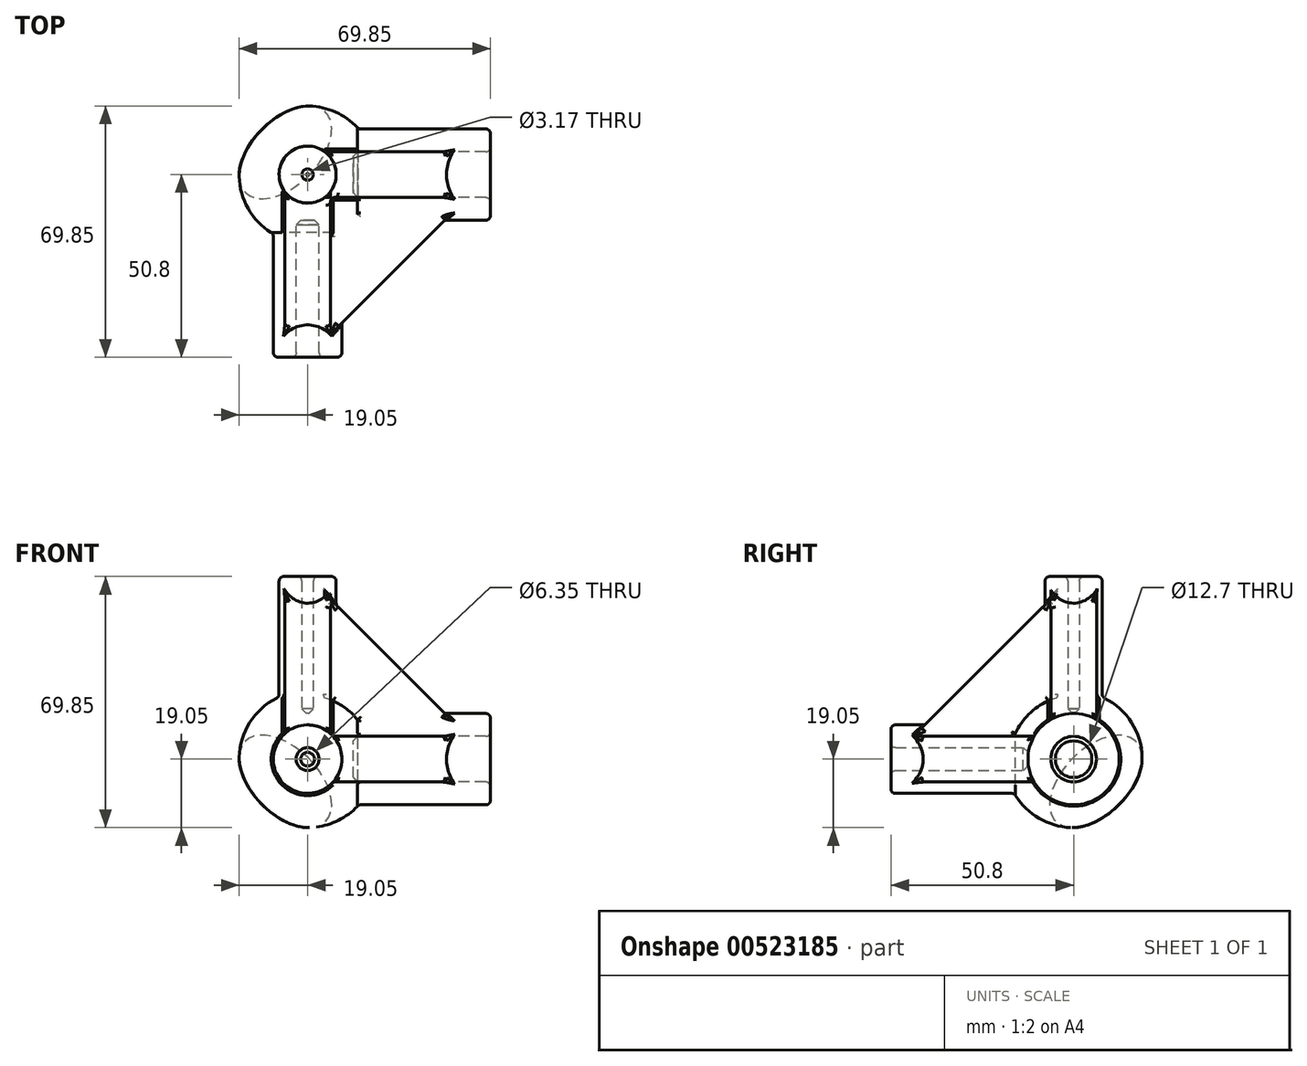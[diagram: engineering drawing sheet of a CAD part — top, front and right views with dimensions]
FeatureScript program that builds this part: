
annotation { "Feature Type Name" : "Feature", "Feature Type Description" : "" }
export const myFeature = defineFeature(function(context is Context, id is Id, definition is map)
    precondition{}
    {
        {
            var Q0;
            Q0=qCreatedBy(makeId("Right.planeOp"),FACE);
            var sketch = newSketch(context, id + "F0", { "sketchPlane" : qUnion([Q0])});
            skLineSegment(sketch, "E0", {"start": v(0, 0) * mm, "end": v(0, 19.05) * mm});
            skLineSegment(sketch, "E1", {"start": v(0, 0) * mm, "end": v(0, -19.05) * mm});
            skLineSegment(sketch, "E2", {"start": v(0, 0) * mm, "end": v(-19.05, 0) * mm});
            skArc(sketch, "E3", {"start": v(0, 19.05) * mm, "mid": v(-19.05, 0) * mm, "end": v(0, -19.05) * mm});
            skSolve(sketch);
        }
        {
            var Q0;
            Q0 = qSketchRegion(id + "F0", true);
            var Q1;
            Q1=sQuery(id+"F0.wireOp",EDGE,"E0");
            revolve(context, id + "F1", {"entities" : qUnion([Q0]), "axis" : qUnion([Q1]), "revolveType" : RevolveType.FULL});
        }
        {
            var Q0;
            Q0=qCreatedBy(makeId("Front.planeOp"),FACE);
            var sketch = newSketch(context, id + "F2", { "sketchPlane" : qUnion([Q0])});
            skCircle(sketch, "E4", {"center": v(0, 0) * mm, "radius": 3.18 * mm});
            skCircle(sketch, "E5.0", {"center": v(0, 0) * mm, "radius": 9.52 * mm});
            skSolve(sketch);
        }
        {
            var Q0;
            Q0 = qSketchRegion(id + "F2", true);
            extrude(context, id + "F3", {"entities" : qUnion([Q0]), "operationType" : NewBodyOperationType.ADD, "depth" : 50.8 * mm, "offsetDistance" : 25.4 * mm});
        }
        {
            var Q0;
            Q0=qCreatedBy(makeId("Right.planeOp"),FACE);
            var sketch = newSketch(context, id + "F4", { "sketchPlane" : qUnion([Q0])});
            skCircle(sketch, "E6", {"center": v(0, 0) * mm, "radius": 6.35 * mm});
            skCircle(sketch, "E7.0", {"center": v(0, 0) * mm, "radius": 12.7 * mm});
            skSolve(sketch);
        }
        {
            var Q0;
            Q0 = qSketchRegion(id + "F4", true);
            extrude(context, id + "F5", {"entities" : qUnion([Q0]), "operationType" : NewBodyOperationType.ADD, "depth" : 50.8 * mm, "offsetDistance" : 25.4 * mm});
        }
        {
            var Q0;
            Q0=qCreatedBy(makeId("Top.planeOp"),FACE);
            var sketch = newSketch(context, id + "F6", { "sketchPlane" : qUnion([Q0])});
            skCircle(sketch, "E8", {"center": v(0, 0) * mm, "radius": 1.59 * mm});
            skCircle(sketch, "E9.0", {"center": v(0, 0) * mm, "radius": 7.94 * mm});
            skSolve(sketch);
        }
        {
            var Q0;
            Q0 = qSketchRegion(id + "F6", true);
            extrude(context, id + "F7", {"entities" : qUnion([Q0]), "operationType" : NewBodyOperationType.ADD, "depth" : 50.8 * mm, "offsetDistance" : 25.4 * mm});
        }
        {
            var Q0;
            Q0=makeQuery(id+"F7.opExtrude","CAP_FACE",FACE,{"disambiguationData":[OSD([sQuery(id+"F6.wireOp",EDGE,"E8"),sQuery(id+"F6.wireOp",EDGE,"E9.0")])],"isStart":false});
            cPlane(context, id + "F8", {"entities" : qUnion([Q0]), "cplaneType" : CPlaneType.OFFSET, "offset" : 0 * mm, "width" : 152.4 * mm, "height" : 152.4 * mm});
        }
        {
            var Q0;
            Q0=qCreatedBy(id+"F8.planeOp",FACE);
            var sketch = newSketch(context, id + "F9", { "sketchPlane" : qUnion([Q0])});
            skCircle(sketch, "E10", {"center": v(0, 0) * mm, "radius": 1.59 * mm});
            skSolve(sketch);
        }
        {
            var Q0;
            Q0=makeQuery(id+"F5.opExtrude","CAP_FACE",FACE,{"disambiguationData":[OSD([sQuery(id+"F4.wireOp",EDGE,"E6"),sQuery(id+"F4.wireOp",EDGE,"E7.0")])],"isStart":false});
            cPlane(context, id + "F10", {"entities" : qUnion([Q0]), "cplaneType" : CPlaneType.OFFSET, "offset" : 0 * mm, "width" : 152.4 * mm, "height" : 152.4 * mm});
        }
        {
            var Q0;
            Q0=qCreatedBy(id+"F10.planeOp",FACE);
            var sketch = newSketch(context, id + "F11", { "sketchPlane" : qUnion([Q0])});
            skCircle(sketch, "E11", {"center": v(0, 0) * mm, "radius": 6.35 * mm});
            skSolve(sketch);
        }
        {
            var Q0;
            Q0=makeQuery(id+"F3.opExtrude","CAP_FACE",FACE,{"disambiguationData":[OSD([sQuery(id+"F2.wireOp",EDGE,"E4"),sQuery(id+"F2.wireOp",EDGE,"E5.0")])],"isStart":false});
            cPlane(context, id + "F12", {"entities" : qUnion([Q0]), "cplaneType" : CPlaneType.OFFSET, "offset" : 0 * mm, "width" : 152.4 * mm, "height" : 152.4 * mm});
        }
        {
            var Q0;
            Q0=qCreatedBy(id+"F12.planeOp",FACE);
            var sketch = newSketch(context, id + "F13", { "sketchPlane" : qUnion([Q0])});
            skCircle(sketch, "E12", {"center": v(0, 0) * mm, "radius": 3.18 * mm});
            skSolve(sketch);
        }
        {
            var Q0;
            Q0=qCreatedBy(makeId("Top.planeOp"),FACE);
            var sketch = newSketch(context, id + "F14", { "sketchPlane" : qUnion([Q0])});
            skLineSegment(sketch, "E13", {"start": v(0, 0) * mm, "end": v(0, 63.5) * mm});
            skLineSegment(sketch, "E14", {"start": v(0, 0) * mm, "end": v(-63.5, 0) * mm});
            skSolve(sketch);
        }
        {
            var Q0;
            Q0=qCreatedBy(makeId("Right.planeOp"),FACE);
            var sketch = newSketch(context, id + "F15", { "sketchPlane" : qUnion([Q0])});
            skPoint(sketch, "E15.0", {"position": v(63.5, 0) * mm});
            skLineSegment(sketch, "E16", {"start": v(0, 0) * mm, "end": v(63.5, 0) * mm});
            skLineSegment(sketch, "E17", {"start": v(0, 0) * mm, "end": v(0, -63.5) * mm});
            skSolve(sketch);
        }
        {
            var Q0;
            Q0=sQuery(id+"F14.wireOp",VERTEX,"E14.end");
            var Q1;
            Q1=sQuery(id+"F15.wireOp",VERTEX,"E15.0");
            var Q2;
            Q2=sQuery(id+"F15.wireOp",VERTEX,"E17.end");
            cPlane(context, id + "F16", {"entities" : qUnion([Q0, Q1, Q2]), "cplaneType" : CPlaneType.THREE_POINT, "offset" : 25.4 * mm, "width" : 152.4 * mm, "height" : 152.4 * mm});
        }
        {
            var Q0;
            Q0=qCreatedBy(id+"F16.planeOp",FACE);
            var sketch = newSketch(context, id + "F17", { "sketchPlane" : qUnion([Q0])});
            skCircle(sketch, "E18", {"center": v(0, 0) * mm, "radius": 25.4 * mm});
            skSolve(sketch);
        }
        {
            var Q0;
            Q0=qCreatedBy(makeId("Top.planeOp"),FACE);
            var sketch = newSketch(context, id + "F18", { "sketchPlane" : qUnion([Q0])});
            skLineSegment(sketch, "E19", {"start": v(0, 0) * mm, "end": v(50.8, 0) * mm});
            skLineSegment(sketch, "E20", {"start": v(0, 0) * mm, "end": v(0, -50.8) * mm});
            skLineSegment(sketch, "E21", {"start": v(50.8, 0) * mm, "end": v(0, -50.8) * mm});
            skSolve(sketch);
        }
        {
            var Q0;
            Q0=makeQuery(id+"F18.imprint","IMPRINT",FACE,{"disambiguationData":[TD([[makeQuery(id+"F18.imprint","IMPRINT",EDGE,{"derivedFrom":sQuery(id+"F18.wireOp",EDGE,"E19")}),-1.0]])]});
            extrude(context, id + "F19", {"entities" : qUnion([Q0]), "operationType" : NewBodyOperationType.ADD, "depth" : 6.35 * mm, "offsetDistance" : 25.4 * mm, "hasDraft" : true, "draftAngle" : 0 * degree, "hasSecondDirection" : true, "secondDirectionOppositeDirection" : true, "secondDirectionDepth" : 6.35 * mm});
        }
        {
            var Q0;
            Q0=makeQuery(id+"F17.imprint","IMPRINT",FACE,{"disambiguationData":[TD([[makeQuery(id+"F17.imprint","IMPRINT",EDGE,{"derivedFrom":sQuery(id+"F17.wireOp",EDGE,"E18")}),1.0]])]});
            extrude(context, id + "F20", {"entities" : qUnion([Q0]), "operationType" : NewBodyOperationType.REMOVE, "depth" : 25.4 * mm, "offsetDistance" : 25.4 * mm});
        }
        {
            var Q0;
            Q0=qCreatedBy(makeId("Right.planeOp"),FACE);
            var sketch = newSketch(context, id + "F21", { "sketchPlane" : qUnion([Q0])});
            skLineSegment(sketch, "E22", {"start": v(0, 0) * mm, "end": v(0, 50.8) * mm});
            skLineSegment(sketch, "E23.0", {"start": v(0, 0) * mm, "end": v(-50.8, 0) * mm});
            skLineSegment(sketch, "E24", {"start": v(0, 50.8) * mm, "end": v(-50.8, 0) * mm});
            skPoint(sketch, "E25.0", {"position": v(0, 0) * mm});
            skLineSegment(sketch, "E26.0", {"start": v(-7.94, 50.8) * mm, "end": v(7.94, 50.8) * mm});
            skLineSegment(sketch, "E26.1", {"start": v(-7.94, 17.32) * mm, "end": v(7.94, 17.32) * mm});
            skSolve(sketch);
        }
        {
            var Q0;
            Q0 = qSketchRegion(id + "F21", true);
            extrude(context, id + "F22", {"entities" : qUnion([Q0]), "operationType" : NewBodyOperationType.ADD, "depth" : 6.35 * mm, "offsetDistance" : 25.4 * mm, "hasSecondDirection" : true, "secondDirectionOppositeDirection" : true, "secondDirectionDepth" : 6.35 * mm});
        }
        {
            var Q0;
            Q0=qCreatedBy(makeId("Front.planeOp"),FACE);
            var sketch = newSketch(context, id + "F23", { "sketchPlane" : qUnion([Q0])});
            skPoint(sketch, "E27.0", {"position": v(50.8, 0) * mm});
            skPoint(sketch, "E28.0", {"position": v(0, 50.8) * mm});
            skLineSegment(sketch, "E29", {"start": v(0, 0) * mm, "end": v(0, 50.8) * mm});
            skLineSegment(sketch, "E30", {"start": v(50.8, 0) * mm, "end": v(0, 50.8) * mm});
            skLineSegment(sketch, "E31", {"start": v(50.8, 0) * mm, "end": v(0, 0) * mm});
            skSolve(sketch);
        }
        {
            var Q0;
            Q0 = qSketchRegion(id + "F23", true);
            extrude(context, id + "F24", {"entities" : qUnion([Q0]), "operationType" : NewBodyOperationType.ADD, "depth" : 6.35 * mm, "offsetDistance" : 25.4 * mm, "hasSecondDirection" : true, "secondDirectionOppositeDirection" : true, "secondDirectionDepth" : 6.35 * mm});
        }
        {
            var Q0;
            Q0 = qSketchRegion(id + "F11", true);
            extrude(context, id + "F25", {"entities" : qUnion([Q0]), "operationType" : NewBodyOperationType.REMOVE, "oppositeDirection" : true, "depth" : 38.1 * mm, "offsetDistance" : 25.4 * mm});
        }
        {
            var Q0;
            Q0 = qSketchRegion(id + "F9", true);
            extrude(context, id + "F26", {"entities" : qUnion([Q0]), "operationType" : NewBodyOperationType.REMOVE, "oppositeDirection" : true, "depth" : 38.1 * mm, "offsetDistance" : 25.4 * mm});
        }
        {
            var Q0;
            Q0 = qSketchRegion(id + "F13", true);
            extrude(context, id + "F27", {"entities" : qUnion([Q0]), "operationType" : NewBodyOperationType.REMOVE, "oppositeDirection" : true, "depth" : 38.1 * mm, "offsetDistance" : 25.4 * mm});
        }
        {
            var Q0;
            {var subQ1=makeQuery(id+"F3.opExtrude","SWEPT_FACE",FACE,{"disambiguationData":[OSD([sQuery(id+"F2.wireOp",EDGE,"E5.0")])]});Q0=makeQuery(id+"F24.boolean.opBoolean","SPLIT",FACE,{"disambiguationData":[TD([makeQuery(id+"F19.opExtrude","CAP_FACE",FACE,{"disambiguationData":[OSD([sQuery(id+"F18.wireOp",EDGE,"E19"),sQuery(id+"F18.wireOp",EDGE,"E20"),sQuery(id+"F18.wireOp",EDGE,"E21")])],"isStart":false})])],"derivedFrom":makeQuery(id+"F7.boolean.opBoolean","SPLIT",FACE,{"disambiguationData":[TD([subQ1])],"derivedFrom":makeQuery(id+"F5.boolean.opBoolean","SPLIT",FACE,{"disambiguationData":[TD([subQ1])],"derivedFrom":makeQuery(id+"F3.boolean.opBoolean","SPLIT",FACE,{"disambiguationData":[TD([subQ1])],"derivedFrom":makeQuery(id+"F1.opRevolve","SWEPT_FACE",FACE,{"disambiguationData":[OSD([sQuery(id+"F0.wireOp",EDGE,"E3")])]})})})})});}
            fillet(context, id + "F28", {"entities" : qUnion([Q0]), "radius" : 1.27 * mm, "tangentPropagation" : true, "allowEdgeOverflow" : false});
        }
        {
            var Q0;
            Q0=makeQuery(id+"F24.boolean.opBoolean","INTERSECT",EDGE,{"derivedFrom":[makeQuery(id+"F5.opExtrude","SWEPT_FACE",FACE,{"disambiguationData":[OSD([sQuery(id+"F4.wireOp",EDGE,"E7.0")])]}),makeQuery(id+"F24.opExtrude","CAP_FACE",FACE,{"disambiguationData":[OSD([sQuery(id+"F23.wireOp",EDGE,"E29"),sQuery(id+"F23.wireOp",EDGE,"E30"),sQuery(id+"F23.wireOp",EDGE,"E31")])],"isStart":false})]});
            var Q1;
            Q1=makeQuery(id+"F19.boolean.opBoolean","INTERSECT",EDGE,{"derivedFrom":[makeQuery(id+"F5.opExtrude","SWEPT_FACE",FACE,{"disambiguationData":[OSD([sQuery(id+"F4.wireOp",EDGE,"E7.0")])]}),makeQuery(id+"F19.opExtrude","CAP_FACE",FACE,{"disambiguationData":[OSD([sQuery(id+"F18.wireOp",EDGE,"E19"),sQuery(id+"F18.wireOp",EDGE,"E20"),sQuery(id+"F18.wireOp",EDGE,"E21")])],"isStart":false})]});
            var Q2;
            Q2=makeQuery(id+"F19.boolean.opBoolean","INTERSECT",EDGE,{"derivedFrom":[makeQuery(id+"F3.opExtrude","SWEPT_FACE",FACE,{"disambiguationData":[OSD([sQuery(id+"F2.wireOp",EDGE,"E5.0")])]}),makeQuery(id+"F19.opExtrude","CAP_FACE",FACE,{"disambiguationData":[OSD([sQuery(id+"F18.wireOp",EDGE,"E19"),sQuery(id+"F18.wireOp",EDGE,"E20"),sQuery(id+"F18.wireOp",EDGE,"E21")])],"isStart":false})]});
            var Q3;
            Q3=makeQuery(id+"F22.boolean.opBoolean","INTERSECT",EDGE,{"derivedFrom":[makeQuery(id+"F3.opExtrude","SWEPT_FACE",FACE,{"disambiguationData":[OSD([sQuery(id+"F2.wireOp",EDGE,"E5.0")])]}),makeQuery(id+"F22.opExtrude","CAP_FACE",FACE,{"disambiguationData":[OSD([sQuery(id+"F21.wireOp",EDGE,"E22"),sQuery(id+"F21.wireOp",EDGE,"E23.0"),sQuery(id+"F21.wireOp",EDGE,"E24")])],"isStart":false})]});
            var Q4;
            Q4=makeQuery(id+"F24.boolean.opBoolean","INTERSECT",EDGE,{"derivedFrom":[makeQuery(id+"F22.opExtrude","CAP_FACE",FACE,{"disambiguationData":[OSD([sQuery(id+"F21.wireOp",EDGE,"E22"),sQuery(id+"F21.wireOp",EDGE,"E23.0"),sQuery(id+"F21.wireOp",EDGE,"E24")])],"isStart":false}),makeQuery(id+"F24.opExtrude","CAP_FACE",FACE,{"disambiguationData":[OSD([sQuery(id+"F23.wireOp",EDGE,"E29"),sQuery(id+"F23.wireOp",EDGE,"E30"),sQuery(id+"F23.wireOp",EDGE,"E31")])],"isStart":false})]});
            fillet(context, id + "F29", {"entities" : qUnion([Q0, Q1, Q2, Q3, Q4]), "radius" : 1.27 * mm, "tangentPropagation" : true, "allowEdgeOverflow" : false});
        }
        {
            var Q0;
            Q0=makeQuery(id+"F22.boolean.opBoolean","INTERSECT",EDGE,{"derivedFrom":[makeQuery(id+"F7.opExtrude","SWEPT_FACE",FACE,{"disambiguationData":[OSD([sQuery(id+"F6.wireOp",EDGE,"E9.0")])]}),makeQuery(id+"F22.opExtrude","CAP_FACE",FACE,{"disambiguationData":[OSD([sQuery(id+"F21.wireOp",EDGE,"E22"),sQuery(id+"F21.wireOp",EDGE,"E23.0"),sQuery(id+"F21.wireOp",EDGE,"E24")])],"isStart":true})]});
            var Q1;
            Q1=makeQuery(id+"F22.boolean.opBoolean","INTERSECT",EDGE,{"derivedFrom":[makeQuery(id+"F3.opExtrude","SWEPT_FACE",FACE,{"disambiguationData":[OSD([sQuery(id+"F2.wireOp",EDGE,"E5.0")])]}),makeQuery(id+"F22.opExtrude","CAP_FACE",FACE,{"disambiguationData":[OSD([sQuery(id+"F21.wireOp",EDGE,"E22"),sQuery(id+"F21.wireOp",EDGE,"E23.0"),sQuery(id+"F21.wireOp",EDGE,"E24")])],"isStart":true})]});
            var Q2;
            {var subQ0=makeQuery(id+"F1.opRevolve","SWEPT_FACE",FACE,{"disambiguationData":[OSD([sQuery(id+"F0.wireOp",EDGE,"E3")])]});var subQ1=makeQuery(id+"F3.opExtrude","SWEPT_FACE",FACE,{"disambiguationData":[OSD([sQuery(id+"F2.wireOp",EDGE,"E5.0")])]});Q2=makeQuery(id+"F22.boolean.opBoolean","SPLIT",EDGE,{"disambiguationData":[TD([makeQuery(id+"F19.opExtrude","CAP_FACE",FACE,{"disambiguationData":[OSD([sQuery(id+"F18.wireOp",EDGE,"E19"),sQuery(id+"F18.wireOp",EDGE,"E20"),sQuery(id+"F18.wireOp",EDGE,"E21")])],"isStart":true})])],"derivedFrom":makeQuery(id+"F3.boolean.opBoolean","INTERSECT",EDGE,{"derivedFrom":[subQ0,subQ1]})});}
            var Q3;
            {var subQ0=makeQuery(id+"F3.opExtrude","SWEPT_FACE",FACE,{"disambiguationData":[OSD([sQuery(id+"F2.wireOp",EDGE,"E5.0")])]});Q3=makeQuery(id+"F22.boolean.opBoolean","INTERSECT",EDGE,{"derivedFrom":[makeQuery(id+"F7.boolean.opBoolean","SPLIT",FACE,{"disambiguationData":[TD([subQ0])],"derivedFrom":makeQuery(id+"F5.boolean.opBoolean","SPLIT",FACE,{"disambiguationData":[TD([subQ0])],"derivedFrom":makeQuery(id+"F3.boolean.opBoolean","SPLIT",FACE,{"disambiguationData":[TD([subQ0])],"derivedFrom":makeQuery(id+"F1.opRevolve","SWEPT_FACE",FACE,{"disambiguationData":[OSD([sQuery(id+"F0.wireOp",EDGE,"E3")])]})})})}),makeQuery(id+"F22.opExtrude","CAP_FACE",FACE,{"disambiguationData":[OSD([sQuery(id+"F21.wireOp",EDGE,"E22"),sQuery(id+"F21.wireOp",EDGE,"E23.0"),sQuery(id+"F21.wireOp",EDGE,"E24")])],"isStart":true})]});}
            var Q4;
            {var subQ0=makeQuery(id+"F3.opExtrude","SWEPT_FACE",FACE,{"disambiguationData":[OSD([sQuery(id+"F2.wireOp",EDGE,"E5.0")])]});Q4=makeQuery(id+"F7.boolean.opBoolean","INTERSECT",EDGE,{"derivedFrom":[makeQuery(id+"F5.boolean.opBoolean","SPLIT",FACE,{"disambiguationData":[TD([subQ0])],"derivedFrom":makeQuery(id+"F3.boolean.opBoolean","SPLIT",FACE,{"disambiguationData":[TD([subQ0])],"derivedFrom":makeQuery(id+"F1.opRevolve","SWEPT_FACE",FACE,{"disambiguationData":[OSD([sQuery(id+"F0.wireOp",EDGE,"E3")])]})})}),makeQuery(id+"F7.opExtrude","SWEPT_FACE",FACE,{"disambiguationData":[OSD([sQuery(id+"F6.wireOp",EDGE,"E9.0")])]})]});}
            var Q5;
            {var subQ0=makeQuery(id+"F3.opExtrude","SWEPT_FACE",FACE,{"disambiguationData":[OSD([sQuery(id+"F2.wireOp",EDGE,"E5.0")])]});Q5=makeQuery(id+"F19.boolean.opBoolean","INTERSECT",EDGE,{"derivedFrom":[makeQuery(id+"F7.boolean.opBoolean","SPLIT",FACE,{"disambiguationData":[TD([subQ0])],"derivedFrom":makeQuery(id+"F5.boolean.opBoolean","SPLIT",FACE,{"disambiguationData":[TD([subQ0])],"derivedFrom":makeQuery(id+"F3.boolean.opBoolean","SPLIT",FACE,{"disambiguationData":[TD([subQ0])],"derivedFrom":makeQuery(id+"F1.opRevolve","SWEPT_FACE",FACE,{"disambiguationData":[OSD([sQuery(id+"F0.wireOp",EDGE,"E3")])]})})})}),makeQuery(id+"F19.opExtrude","CAP_FACE",FACE,{"disambiguationData":[OSD([sQuery(id+"F18.wireOp",EDGE,"E19"),sQuery(id+"F18.wireOp",EDGE,"E20"),sQuery(id+"F18.wireOp",EDGE,"E21")])],"isStart":true})]});}
            var Q6;
            Q6=makeQuery(id+"F19.boolean.opBoolean","INTERSECT",EDGE,{"derivedFrom":[makeQuery(id+"F3.opExtrude","SWEPT_FACE",FACE,{"disambiguationData":[OSD([sQuery(id+"F2.wireOp",EDGE,"E5.0")])]}),makeQuery(id+"F19.opExtrude","CAP_FACE",FACE,{"disambiguationData":[OSD([sQuery(id+"F18.wireOp",EDGE,"E19"),sQuery(id+"F18.wireOp",EDGE,"E20"),sQuery(id+"F18.wireOp",EDGE,"E21")])],"isStart":true})]});
            var Q7;
            Q7=makeQuery(id+"F19.boolean.opBoolean","INTERSECT",EDGE,{"derivedFrom":[makeQuery(id+"F5.opExtrude","SWEPT_FACE",FACE,{"disambiguationData":[OSD([sQuery(id+"F4.wireOp",EDGE,"E7.0")])]}),makeQuery(id+"F19.opExtrude","CAP_FACE",FACE,{"disambiguationData":[OSD([sQuery(id+"F18.wireOp",EDGE,"E19"),sQuery(id+"F18.wireOp",EDGE,"E20"),sQuery(id+"F18.wireOp",EDGE,"E21")])],"isStart":true})]});
            var Q8;
            {var subQ0=makeQuery(id+"F1.opRevolve","SWEPT_FACE",FACE,{"disambiguationData":[OSD([sQuery(id+"F0.wireOp",EDGE,"E3")])]});var subQ1=makeQuery(id+"F5.opExtrude","SWEPT_FACE",FACE,{"disambiguationData":[OSD([sQuery(id+"F4.wireOp",EDGE,"E7.0")])]});Q8=makeQuery(id+"F24.boolean.opBoolean","SPLIT",EDGE,{"disambiguationData":[TD([makeQuery(id+"F19.opExtrude","CAP_FACE",FACE,{"disambiguationData":[OSD([sQuery(id+"F18.wireOp",EDGE,"E19"),sQuery(id+"F18.wireOp",EDGE,"E20"),sQuery(id+"F18.wireOp",EDGE,"E21")])],"isStart":true})])],"derivedFrom":makeQuery(id+"F5.boolean.opBoolean","INTERSECT",EDGE,{"derivedFrom":[makeQuery(id+"F3.boolean.opBoolean","SPLIT",FACE,{"disambiguationData":[TD([makeQuery(id+"F3.opExtrude","SWEPT_FACE",FACE,{"disambiguationData":[OSD([sQuery(id+"F2.wireOp",EDGE,"E5.0")])]})])],"derivedFrom":subQ0}),subQ1]})});}
            var Q9;
            {var subQ0=makeQuery(id+"F3.opExtrude","SWEPT_FACE",FACE,{"disambiguationData":[OSD([sQuery(id+"F2.wireOp",EDGE,"E5.0")])]});Q9=makeQuery(id+"F24.boolean.opBoolean","INTERSECT",EDGE,{"derivedFrom":[makeQuery(id+"F7.boolean.opBoolean","SPLIT",FACE,{"disambiguationData":[TD([subQ0])],"derivedFrom":makeQuery(id+"F5.boolean.opBoolean","SPLIT",FACE,{"disambiguationData":[TD([subQ0])],"derivedFrom":makeQuery(id+"F3.boolean.opBoolean","SPLIT",FACE,{"disambiguationData":[TD([subQ0])],"derivedFrom":makeQuery(id+"F1.opRevolve","SWEPT_FACE",FACE,{"disambiguationData":[OSD([sQuery(id+"F0.wireOp",EDGE,"E3")])]})})})}),makeQuery(id+"F24.opExtrude","CAP_FACE",FACE,{"disambiguationData":[OSD([sQuery(id+"F23.wireOp",EDGE,"E29"),sQuery(id+"F23.wireOp",EDGE,"E30"),sQuery(id+"F23.wireOp",EDGE,"E31")])],"isStart":true})]});}
            var Q10;
            Q10=makeQuery(id+"F24.boolean.opBoolean","INTERSECT",EDGE,{"derivedFrom":[makeQuery(id+"F7.opExtrude","SWEPT_FACE",FACE,{"disambiguationData":[OSD([sQuery(id+"F6.wireOp",EDGE,"E9.0")])]}),makeQuery(id+"F24.opExtrude","CAP_FACE",FACE,{"disambiguationData":[OSD([sQuery(id+"F23.wireOp",EDGE,"E29"),sQuery(id+"F23.wireOp",EDGE,"E30"),sQuery(id+"F23.wireOp",EDGE,"E31")])],"isStart":true})]});
            var Q11;
            Q11=makeQuery(id+"F24.boolean.opBoolean","INTERSECT",EDGE,{"derivedFrom":[makeQuery(id+"F5.opExtrude","SWEPT_FACE",FACE,{"disambiguationData":[OSD([sQuery(id+"F4.wireOp",EDGE,"E7.0")])]}),makeQuery(id+"F24.opExtrude","CAP_FACE",FACE,{"disambiguationData":[OSD([sQuery(id+"F23.wireOp",EDGE,"E29"),sQuery(id+"F23.wireOp",EDGE,"E30"),sQuery(id+"F23.wireOp",EDGE,"E31")])],"isStart":true})]});
            var Q12;
            Q12=makeQuery(id+"F24.boolean.opBoolean","INTERSECT",EDGE,{"disambiguationData":[OD(0.0)],"derivedFrom":[makeQuery(id+"F7.opExtrude","SWEPT_FACE",FACE,{"disambiguationData":[OSD([sQuery(id+"F6.wireOp",EDGE,"E9.0")])]}),makeQuery(id+"F24.opExtrude","SWEPT_FACE",FACE,{"disambiguationData":[OSD([sQuery(id+"F23.wireOp",EDGE,"E30")])]})]});
            var Q13;
            Q13=makeQuery(id+"F24.boolean.opBoolean","INTERSECT",EDGE,{"derivedFrom":[makeQuery(id+"F5.opExtrude","SWEPT_FACE",FACE,{"disambiguationData":[OSD([sQuery(id+"F4.wireOp",EDGE,"E7.0")])]}),makeQuery(id+"F24.opExtrude","SWEPT_FACE",FACE,{"disambiguationData":[OSD([sQuery(id+"F23.wireOp",EDGE,"E30")])]})]});
            var Q14;
            {var subQ0=makeQuery(id+"F19.opExtrude","SWEPT_FACE",FACE,{"disambiguationData":[OSD([sQuery(id+"F18.wireOp",EDGE,"E21")])]});Q14=makeQuery(id+"F19.boolean.opBoolean","INTERSECT",EDGE,{"derivedFrom":[makeQuery(id+"F5.opExtrude","SWEPT_FACE",FACE,{"disambiguationData":[OSD([sQuery(id+"F4.wireOp",EDGE,"E7.0")])]}),makeQuery(id+"F19.*.booleanUnion.opBoolean","MERGE",FACE,{"derivedFrom":[makeQuery(id+"F19.*.split.splitOp","SPLIT",FACE,{"derivedFrom":subQ0,"isFromBackBody":true}),makeQuery(id+"F19.*.split.splitOp","SPLIT",FACE,{"derivedFrom":subQ0})]})]});}
            var Q15;
            {var subQ0=makeQuery(id+"F19.opExtrude","SWEPT_FACE",FACE,{"disambiguationData":[OSD([sQuery(id+"F18.wireOp",EDGE,"E21")])]});Q15=makeQuery(id+"F19.boolean.opBoolean","INTERSECT",EDGE,{"derivedFrom":[makeQuery(id+"F3.opExtrude","SWEPT_FACE",FACE,{"disambiguationData":[OSD([sQuery(id+"F2.wireOp",EDGE,"E5.0")])]}),makeQuery(id+"F19.*.booleanUnion.opBoolean","MERGE",FACE,{"derivedFrom":[makeQuery(id+"F19.*.split.splitOp","SPLIT",FACE,{"derivedFrom":subQ0,"isFromBackBody":true}),makeQuery(id+"F19.*.split.splitOp","SPLIT",FACE,{"derivedFrom":subQ0})]})]});}
            var Q16;
            Q16=makeQuery(id+"F22.boolean.opBoolean","INTERSECT",EDGE,{"derivedFrom":[makeQuery(id+"F3.opExtrude","SWEPT_FACE",FACE,{"disambiguationData":[OSD([sQuery(id+"F2.wireOp",EDGE,"E5.0")])]}),makeQuery(id+"F22.opExtrude","SWEPT_FACE",FACE,{"disambiguationData":[OSD([sQuery(id+"F21.wireOp",EDGE,"E24")])]})]});
            var Q17;
            {var subQ0=makeQuery(id+"F7.opExtrude","SWEPT_FACE",FACE,{"disambiguationData":[OSD([sQuery(id+"F6.wireOp",EDGE,"E9.0")])]});var subQ1=sQuery(id+"F21.wireOp",EDGE,"E24");var subQ2=makeQuery(id+"F22.opExtrude","SWEPT_FACE",FACE,{"disambiguationData":[OSD([subQ1])]});Q17=makeQuery(id+"F24.boolean.opBoolean","SPLIT",EDGE,{"disambiguationData":[TD([makeQuery(id+"F22.opExtrude","CAP_FACE",FACE,{"disambiguationData":[OSD([sQuery(id+"F21.wireOp",EDGE,"E22"),sQuery(id+"F21.wireOp",EDGE,"E23.0"),subQ1])],"isStart":true})])],"derivedFrom":makeQuery(id+"F22.boolean.opBoolean","INTERSECT",EDGE,{"derivedFrom":[subQ0,subQ2]})});}
            fillet(context, id + "F30", {"entities" : qUnion([Q0, Q1, Q2, Q3, Q4, Q5, Q6, Q7, Q8, Q9, Q10, Q11, Q12, Q13, Q14, Q15, Q16, Q17]), "radius" : 1.27 * mm, "tangentPropagation" : true, "allowEdgeOverflow" : false});
        }
        {
            var Q0;
            Q0=makeQuery(id+"F25.boolean.opBoolean","COPY",EDGE,{"derivedFrom":makeQuery(id+"F25.opExtrude","CAP_EDGE",EDGE,{"disambiguationData":[OSD([sQuery(id+"F11.wireOp",EDGE,"E11")])],"isStart":false})});
            var Q1;
            Q1=makeQuery(id+"F27.boolean.opBoolean","COPY",EDGE,{"derivedFrom":makeQuery(id+"F27.opExtrude","CAP_EDGE",EDGE,{"disambiguationData":[OSD([sQuery(id+"F13.wireOp",EDGE,"E12")])],"isStart":false})});
            var Q2;
            Q2=makeQuery(id+"F26.boolean.opBoolean","COPY",EDGE,{"derivedFrom":makeQuery(id+"F26.opExtrude","CAP_EDGE",EDGE,{"disambiguationData":[OSD([sQuery(id+"F9.wireOp",EDGE,"E10")])],"isStart":false})});
            chamfer(context, id + "F31", {"entities" : qUnion([Q0, Q1, Q2]), "width" : 1.27 * mm, "tangentPropagation" : true});
        }
        {
            var Q0;
            {var subQ0=sQuery(id+"F23.wireOp",EDGE,"E30");Q0=makeQuery(id+"F24.boolean.opBoolean","SPLIT",EDGE,{"disambiguationData":[TD([makeQuery(id+"F5.opExtrude","SWEPT_FACE",FACE,{"disambiguationData":[OSD([sQuery(id+"F4.wireOp",EDGE,"E7.0")])]})])],"derivedFrom":makeQuery(id+"F24.opExtrude","CAP_EDGE",EDGE,{"disambiguationData":[OSD([subQ0])],"isStart":false})});}
            var Q1;
            Q1=makeQuery(id+"F24.opExtrude","CAP_EDGE",EDGE,{"disambiguationData":[OSD([sQuery(id+"F23.wireOp",EDGE,"E30")])],"isStart":true});
            var Q2;
            Q2=makeQuery(id+"F19.opExtrude","CAP_EDGE",EDGE,{"disambiguationData":[OSD([sQuery(id+"F18.wireOp",EDGE,"E21")])],"isStart":false});
            var Q3;
            Q3=makeQuery(id+"F19.opExtrude","CAP_EDGE",EDGE,{"disambiguationData":[OSD([sQuery(id+"F18.wireOp",EDGE,"E21")])],"isStart":true});
            var Q4;
            Q4=makeQuery(id+"F22.opExtrude","CAP_EDGE",EDGE,{"disambiguationData":[OSD([sQuery(id+"F21.wireOp",EDGE,"E24")])],"isStart":true});
            var Q5;
            {var subQ0=sQuery(id+"F21.wireOp",EDGE,"E24");Q5=makeQuery(id+"F24.boolean.opBoolean","SPLIT",EDGE,{"disambiguationData":[TD([makeQuery(id+"F3.opExtrude","SWEPT_FACE",FACE,{"disambiguationData":[OSD([sQuery(id+"F2.wireOp",EDGE,"E5.0")])]})])],"derivedFrom":makeQuery(id+"F22.opExtrude","CAP_EDGE",EDGE,{"disambiguationData":[OSD([subQ0])],"isStart":false})});}
            fillet(context, id + "F32", {"entities" : qUnion([Q0, Q1, Q2, Q3, Q4, Q5]), "radius" : 1.27 * mm, "tangentPropagation" : true, "allowEdgeOverflow" : false});
        }
        {
            var Q0;
            Q0=makeQuery(id+"F7.opExtrude","CAP_EDGE",EDGE,{"disambiguationData":[OSD([sQuery(id+"F6.wireOp",EDGE,"E9.0")])],"isStart":false});
            var Q1;
            {var subQ0=makeQuery(id+"F7.opExtrude","CAP_EDGE",EDGE,{"disambiguationData":[OSD([sQuery(id+"F6.wireOp",EDGE,"E8")])],"isStart":false});var subQ1=makeQuery(id+"F22.boolean.opBoolean","SPLIT",EDGE,{"disambiguationData":[OD(1.0)],"derivedFrom":subQ0});var subQ2=makeQuery(id+"F22.boolean.opBoolean","SPLIT",EDGE,{"disambiguationData":[OD(0.0)],"derivedFrom":subQ0});Q1=makeQuery(id+"F26.boolean.opBoolean","MERGE",EDGE,{"derivedFrom":[makeQuery(id+"F24.boolean.opBoolean","SPLIT",EDGE,{"disambiguationData":[OD(0.0)],"derivedFrom":subQ2}),makeQuery(id+"F24.boolean.opBoolean","SPLIT",EDGE,{"disambiguationData":[OD(1.0)],"derivedFrom":subQ2}),makeQuery(id+"F24.boolean.opBoolean","SPLIT",EDGE,{"disambiguationData":[OD(0.0)],"derivedFrom":subQ1}),makeQuery(id+"F24.boolean.opBoolean","SPLIT",EDGE,{"disambiguationData":[OD(1.0)],"derivedFrom":subQ1})]});}
            var Q2;
            {var subQ0=makeQuery(id+"F5.opExtrude","CAP_EDGE",EDGE,{"disambiguationData":[OSD([sQuery(id+"F4.wireOp",EDGE,"E6")])],"isStart":false});var subQ1=makeQuery(id+"F19.boolean.opBoolean","SPLIT",EDGE,{"disambiguationData":[OD(1.0)],"derivedFrom":subQ0});var subQ2=makeQuery(id+"F19.boolean.opBoolean","SPLIT",EDGE,{"disambiguationData":[OD(0.0)],"derivedFrom":subQ0});Q2=makeQuery(id+"F25.boolean.opBoolean","MERGE",EDGE,{"derivedFrom":[makeQuery(id+"F24.boolean.opBoolean","SPLIT",EDGE,{"disambiguationData":[OD(0.0)],"derivedFrom":subQ2}),makeQuery(id+"F24.boolean.opBoolean","SPLIT",EDGE,{"disambiguationData":[OD(1.0)],"derivedFrom":subQ2}),makeQuery(id+"F24.boolean.opBoolean","SPLIT",EDGE,{"disambiguationData":[OD(0.0)],"derivedFrom":subQ1}),makeQuery(id+"F24.boolean.opBoolean","SPLIT",EDGE,{"disambiguationData":[OD(1.0)],"derivedFrom":subQ1})]});}
            var Q3;
            Q3=makeQuery(id+"F5.opExtrude","CAP_EDGE",EDGE,{"disambiguationData":[OSD([sQuery(id+"F4.wireOp",EDGE,"E7.0")])],"isStart":false});
            var Q4;
            {var subQ0=makeQuery(id+"F3.opExtrude","CAP_EDGE",EDGE,{"disambiguationData":[OSD([sQuery(id+"F2.wireOp",EDGE,"E4")])],"isStart":false});var subQ1=makeQuery(id+"F19.boolean.opBoolean","SPLIT",EDGE,{"disambiguationData":[OD(1.0)],"derivedFrom":subQ0});var subQ2=makeQuery(id+"F19.boolean.opBoolean","SPLIT",EDGE,{"disambiguationData":[OD(0.0)],"derivedFrom":subQ0});Q4=makeQuery(id+"F27.boolean.opBoolean","MERGE",EDGE,{"derivedFrom":[makeQuery(id+"F22.boolean.opBoolean","SPLIT",EDGE,{"disambiguationData":[OD(0.0)],"derivedFrom":subQ2}),makeQuery(id+"F22.boolean.opBoolean","SPLIT",EDGE,{"disambiguationData":[OD(1.0)],"derivedFrom":subQ2}),makeQuery(id+"F22.boolean.opBoolean","SPLIT",EDGE,{"disambiguationData":[OD(0.0)],"derivedFrom":subQ1}),makeQuery(id+"F22.boolean.opBoolean","SPLIT",EDGE,{"disambiguationData":[OD(1.0)],"derivedFrom":subQ1})]});}
            var Q5;
            Q5=makeQuery(id+"F3.opExtrude","CAP_EDGE",EDGE,{"disambiguationData":[OSD([sQuery(id+"F2.wireOp",EDGE,"E5.0")])],"isStart":false});
            var Q6;
            {var subQ0=makeQuery(id+"F3.opExtrude","SWEPT_FACE",FACE,{"disambiguationData":[OSD([sQuery(id+"F2.wireOp",EDGE,"E5.0")])]});Q6=makeQuery(id+"F20.boolean.opBoolean","INTERSECT",EDGE,{"derivedFrom":[makeQuery(id+"F7.boolean.opBoolean","SPLIT",FACE,{"disambiguationData":[TD([subQ0])],"derivedFrom":makeQuery(id+"F5.boolean.opBoolean","SPLIT",FACE,{"disambiguationData":[TD([subQ0])],"derivedFrom":makeQuery(id+"F3.boolean.opBoolean","SPLIT",FACE,{"disambiguationData":[TD([subQ0])],"derivedFrom":makeQuery(id+"F1.opRevolve","SWEPT_FACE",FACE,{"disambiguationData":[OSD([sQuery(id+"F0.wireOp",EDGE,"E3")])]})})})}),makeQuery(id+"F20.opExtrude","CAP_FACE",FACE,{"disambiguationData":[OSD([sQuery(id+"F17.wireOp",EDGE,"E18")])],"isStart":false})]});}
            fillet(context, id + "F33", {"entities" : qUnion([Q0, Q1, Q2, Q3, Q4, Q5, Q6]), "radius" : 1.27 * mm, "tangentPropagation" : true, "allowEdgeOverflow" : false});
        }
    });
